# Revit family: 304_Cim3739B-_
name_source: partatom
category: Pipe Accessories
revit_build: Autodesk Revit 2017 (Build: 20160225_1515(x64)
units: mm (PartAtom-declared; Revit-internal decimal feet)

## family parameters
Always vertical = Yes
Cut with Voids When Loaded = No
Part Type = Valve - Breaks Into
Round Connector Dimension = Use Diameter
Shared = No
Work Plane-Based = No

## types (10) — shared parameters
CAT0 = Yes
Description = BALANCING VALVE - VARIABLE ORIFICE - PN 16 - CAST IRON - FLANGED END
HH6 = 35 mm  [stored 0.114829 ft]
HH9 = 20 mm  [stored 0.0656168 ft]
L2D_Min = 3048 mm
Manufacturer = Cimberio
QmdConnectorList = 301;D;302;D
URL = www.cimberio.it
magiPartTypeId = 304
magiProductFamilyId = Cim3739B-*
zero-valued in all types: MC_Default_elevation

## per-type parameters (varying)
| type | CAT1 | CAT2 | D | D1 | DD1 | DD3 | DD4 | DD5 | E | G | GG1 | HH1 | HH4 | HH5 | HH7 | HH8 | L2D | LL1 | LL2 | LL3 | LL5 | S | S__ve | W2D |
| Cim3739B-40 | Yes | No | 40 mm | 100 mm | 76 mm | 50 mm  [stored 0.164042 ft] | 23 mm | 231 mm | 165 mm | 100 mm | 80 mm  [stored 0.262467 ft] | 158 mm | 158 mm | 50 mm  [stored 0.164042 ft] | 40 mm  [stored 0.131234 ft] | 237 mm | 200 mm | 100 mm | 160 mm | 93 mm | 60 mm | 20 mm  [stored 0.0656168 ft] | -20 mm  [stored -0.0656168 ft] | 40 mm  [stored 0.131234 ft] |
| Cim3739B-300 | No | Yes | 300 mm | 425 mm | 212 mm | 138 mm | 64 mm | 644 mm | 460 mm | 370 mm | 296 mm | 684 mm | 684 mm | 213 mm | 434 mm | 553 mm | 850 mm | 425 mm | 786 mm | 334 mm | 255 mm | 32 mm  [stored 0.104987 ft] | -32 mm  [stored -0.104987 ft] | 300 mm |
| Cim3739B-250 | No | Yes | 250 mm | 365 mm | 186 mm | 122 mm | 57 mm | 567 mm | 405 mm | 319 mm | 255 mm | 666 mm | 666 mm | 183 mm | 441 mm | 522 mm | 730 mm | 365 mm | 666 mm | 363 mm | 219 mm | 32 mm  [stored 0.104987 ft] | -32 mm  [stored -0.104987 ft] | 250 mm |
| Cim3739B-200 | No | Yes | 200 mm | 300 mm | 156 mm | 102 mm | 48 mm | 476 mm | 340 mm | 266 mm | 213 mm | 623 mm | 623 mm | 150 mm | 430 mm | 474 mm | 600 mm | 300 mm | 540 mm | 363 mm | 180 mm | 30 mm  [stored 0.0984252 ft] | -30 mm  [stored -0.0984252 ft] | 200 mm |
| Cim3739B-150 | Yes | No | 150 mm | 240 mm | 131 mm | 86 mm | 40 mm  [stored 0.131234 ft] | 399 mm | 285 mm | 211 mm | 169 mm | 371 mm | 371 mm | 120 mm | 203 mm | 361 mm | 480 mm | 240 mm | 428 mm | 224 mm | 144 mm | 26 mm  [stored 0.0853018 ft] | -26 mm  [stored -0.0853018 ft] | 150 mm |
| Cim3739B-125 | Yes | No | 125 mm | 200 mm | 115 mm | 75 mm  [stored 0.246063 ft] | 35 mm  [stored 0.114829 ft] | 350 mm | 250 mm | 178 mm | 142 mm | 356 mm | 356 mm | 100 mm | 203 mm | 341 mm | 400 mm | 200 mm | 348 mm | 238 mm | 120 mm | 26 mm  [stored 0.0853018 ft] | -26 mm  [stored -0.0853018 ft] | 125 mm |
| Cim3739B-100 | Yes | No | 100 mm | 175 mm | 101 mm | 66 mm  [stored 0.216535 ft] | 31 mm | 308 mm | 220 mm | 156 mm | 125 mm | 302 mm | 302 mm | 88 mm | 167 mm | 304 mm | 350 mm | 175 mm | 302 mm | 193 mm | 105 mm | 24 mm  [stored 0.0787402 ft] | -24 mm  [stored -0.0787402 ft] | 100 mm |
| Cim3739B-80 | Yes | No | 80 mm | 155 mm | 92 mm  [stored 0.301837 ft] | 60 mm | 28 mm  [stored 0.0918635 ft] | 280 mm | 200 mm | 132 mm | 106 mm | 193 mm | 193 mm | 78 mm | 68 mm | 256 mm | 310 mm | 155 mm | 266 mm | 108 mm | 93 mm | 22 mm  [stored 0.0721785 ft] | -22 mm  [stored -0.0721785 ft] | 80 mm  [stored 0.262467 ft] |
| Cim3739B-65 | Yes | No | 65 mm | 145 mm | 85 mm | 56 mm | 26 mm  [stored 0.0853018 ft] | 259 mm | 185 mm | 118 mm | 94 mm | 182 mm | 182 mm | 73 mm | 67 mm | 242 mm | 290 mm | 145 mm | 250 mm | 102 mm | 87 mm  [stored 0.285433 ft] | 20 mm  [stored 0.0656168 ft] | -20 mm  [stored -0.0656168 ft] | 65 mm  [stored 0.213255 ft] |
| Cim3739B-50 | Yes | No | 50 mm | 115 mm | 76 mm | 50 mm  [stored 0.164042 ft] | 23 mm | 231 mm | 165 mm | 100 mm | 80 mm  [stored 0.262467 ft] | 158 mm | 158 mm | 58 mm | 48 mm | 229 mm | 230 mm | 115 mm | 190 mm | 95 mm | 69 mm  [stored 0.226378 ft] | 20 mm  [stored 0.0656168 ft] | -20 mm  [stored -0.0656168 ft] | 50 mm  [stored 0.164042 ft] |

note: column(s) folded — value = type name in every type: magiProductCode, magiProductId

note: [stored X ft] marks values corroborated as IEEE doubles in the binary element streams (Revit-internal decimal feet)

## geometry (parser evidence)
native form markers: Sweep x2
no freeform markers — native parametric forms only
